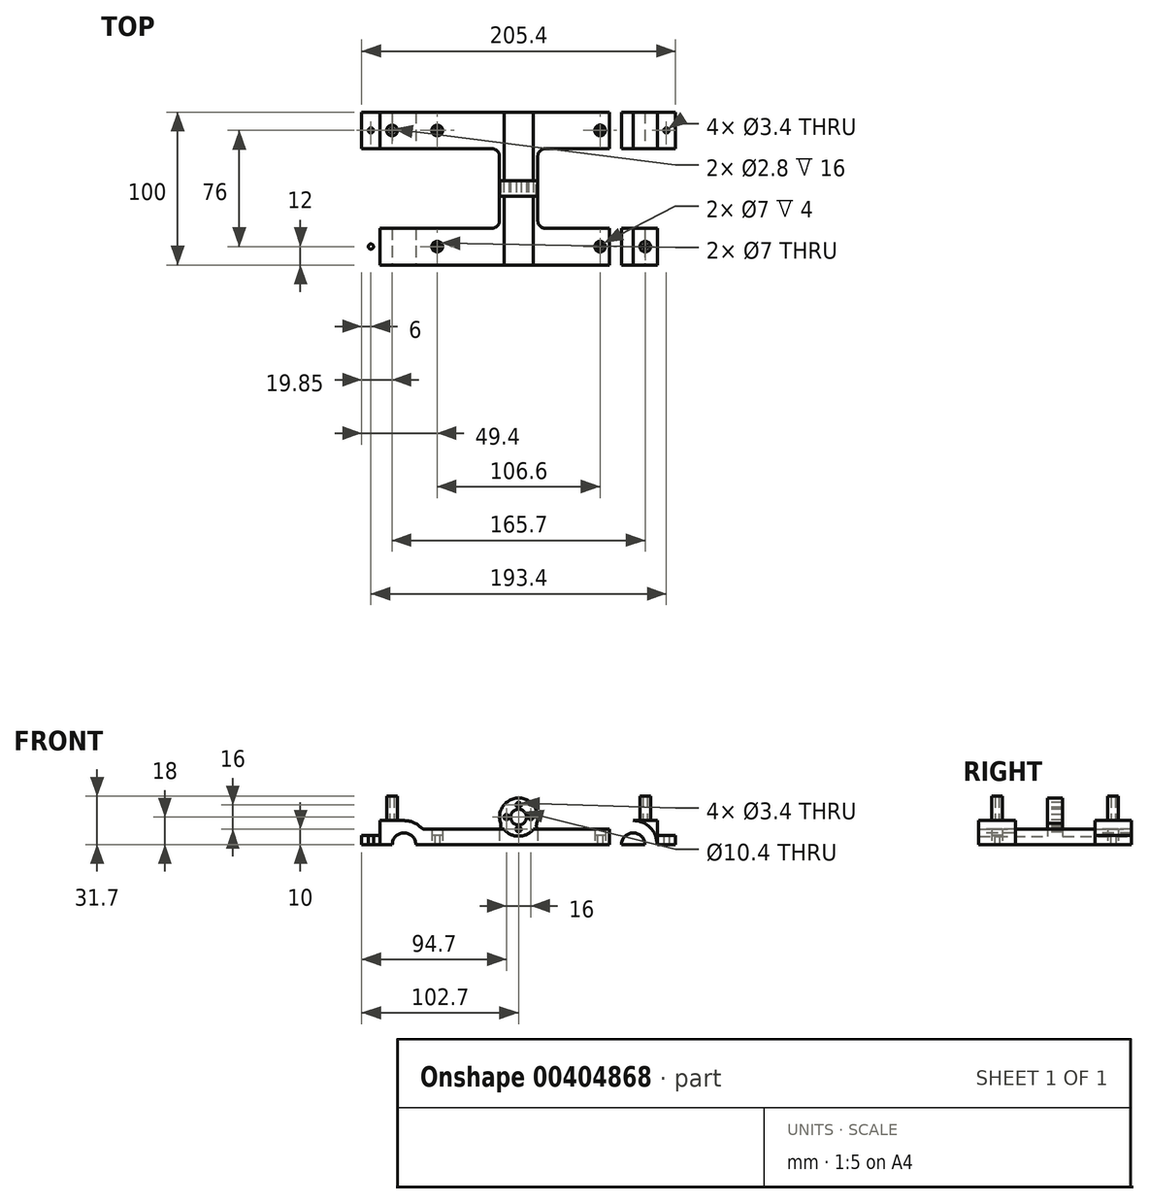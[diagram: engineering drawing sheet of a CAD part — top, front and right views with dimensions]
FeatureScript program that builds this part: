
annotation { "Feature Type Name" : "Feature", "Feature Type Description" : "" }
export const myFeature = defineFeature(function(context is Context, id is Id, definition is map)
    precondition{}
    {
        {
            var Q0;
            Q0=qCreatedBy(makeId("Top.planeOp"),FACE);
            var sketch = newSketch(context, id + "F0", { "sketchPlane" : qUnion([Q0])});
            skLineSegment(sketch, "E0", {"start": v(0, 0) * mm, "end": v(0, 50) * mm, "construction": true});
            skLineSegment(sketch, "E1", {"start": v(0, 0) * mm, "end": v(0, -50) * mm, "construction": true});
            skLineSegment(sketch, "E2", {"start": v(0, 50) * mm, "end": v(-59.3, 50) * mm});
            skLineSegment(sketch, "E3", {"start": v(-59.3, 50) * mm, "end": v(-59.3, 26) * mm});
            skLineSegment(sketch, "E4.bottom", {"start": v(-59.3, 26) * mm, "end": v(-90.7, 26) * mm});
            skLineSegment(sketch, "E4.top", {"start": v(-59.3, 50) * mm, "end": v(-90.7, 50) * mm});
            skLineSegment(sketch, "E4.left", {"start": v(-59.3, 26) * mm, "end": v(-59.3, 50) * mm});
            skLineSegment(sketch, "E4.right", {"start": v(-90.7, 26) * mm, "end": v(-90.7, 50) * mm});
            skLineSegment(sketch, "E5", {"start": v(-59.3, 26) * mm, "end": v(-12.5, 26) * mm});
            skLineSegment(sketch, "E6", {"start": v(0, 0) * mm, "end": v(-12.5, 0) * mm, "construction": true});
            skLineSegment(sketch, "E7", {"start": v(-12.5, 0) * mm, "end": v(-12.5, 26) * mm});
            skLineSegment(sketch, "E8.MirrorCS", {"start": v(59.3, 50) * mm, "end": v(90.7, 50) * mm});
            skLineSegment(sketch, "E9.MirrorCS", {"start": v(90.7, 26) * mm, "end": v(90.7, 50) * mm});
            skLineSegment(sketch, "E10.MirrorCS", {"start": v(59.3, 26) * mm, "end": v(90.7, 26) * mm});
            skLineSegment(sketch, "E11.MirrorCS", {"start": v(59.3, 26) * mm, "end": v(59.3, 50) * mm});
            skLineSegment(sketch, "E12.MirrorCS", {"start": v(59.3, 26) * mm, "end": v(12.5, 26) * mm});
            skLineSegment(sketch, "E13.MirrorCS", {"start": v(0, 50) * mm, "end": v(59.3, 50) * mm});
            skLineSegment(sketch, "E14.MirrorCS", {"start": v(12.5, 0) * mm, "end": v(12.5, 26) * mm});
            skLineSegment(sketch, "E15.MirrorCS", {"start": v(-12.5, 0) * mm, "end": v(-12.5, -26) * mm});
            skLineSegment(sketch, "E16.MirrorCS", {"start": v(-59.3, -26) * mm, "end": v(-12.5, -26) * mm});
            skLineSegment(sketch, "E17.MirrorCS", {"start": v(-59.3, -26) * mm, "end": v(-90.7, -26) * mm});
            skLineSegment(sketch, "E18.MirrorCS", {"start": v(-90.7, -26) * mm, "end": v(-90.7, -50) * mm});
            skLineSegment(sketch, "E19.MirrorCS", {"start": v(-59.3, -50) * mm, "end": v(-90.7, -50) * mm});
            skLineSegment(sketch, "E20.MirrorCS", {"start": v(-59.3, -26) * mm, "end": v(-59.3, -50) * mm});
            skLineSegment(sketch, "E21.MirrorCS", {"start": v(0, -50) * mm, "end": v(-59.3, -50) * mm});
            skLineSegment(sketch, "E22.MirrorCS", {"start": v(0, -50) * mm, "end": v(59.3, -50) * mm});
            skLineSegment(sketch, "E23.MirrorCS", {"start": v(59.3, -26) * mm, "end": v(12.5, -26) * mm});
            skLineSegment(sketch, "E24.MirrorCS", {"start": v(12.5, 0) * mm, "end": v(12.5, -26) * mm});
            skLineSegment(sketch, "E25.MirrorCS", {"start": v(59.3, -26) * mm, "end": v(90.7, -26) * mm});
            skLineSegment(sketch, "E26.MirrorCS", {"start": v(59.3, -26) * mm, "end": v(59.3, -50) * mm});
            skLineSegment(sketch, "E27.MirrorCS", {"start": v(59.3, -50) * mm, "end": v(90.7, -50) * mm});
            skLineSegment(sketch, "E28.MirrorCS", {"start": v(90.7, -26) * mm, "end": v(90.7, -50) * mm});
            skLineSegment(sketch, "E29.bottom", {"start": v(-12.5, 5) * mm, "end": v(12.5, 5) * mm});
            skLineSegment(sketch, "E29.top", {"start": v(-12.5, -5) * mm, "end": v(12.5, -5) * mm});
            skLineSegment(sketch, "E29.left", {"start": v(-12.5, 5) * mm, "end": v(-12.5, -5) * mm});
            skLineSegment(sketch, "E29.right", {"start": v(12.5, 5) * mm, "end": v(12.5, -5) * mm});
            skPoint(sketch, "E29.middle", {"position": v(0, 0) * mm});
            skLineSegment(sketch, "E30.bottom", {"start": v(-90.7, 50) * mm, "end": v(-102.7, 50) * mm});
            skLineSegment(sketch, "E30.top", {"start": v(-90.7, 26) * mm, "end": v(-102.7, 26) * mm});
            skLineSegment(sketch, "E30.left", {"start": v(-90.7, 50) * mm, "end": v(-90.7, 26) * mm});
            skLineSegment(sketch, "E30.right", {"start": v(-102.7, 50) * mm, "end": v(-102.7, 26) * mm});
            skCircle(sketch, "E31", {"center": v(-96.7, 38) * mm, "radius": 1.7 * mm});
            skPoint(sketch, "E31.centerSnap0", {"position": v(-90.7, 38) * mm});
            skPoint(sketch, "E31.centerSnap1", {"position": v(-96.7, 50) * mm});
            skLineSegment(sketch, "E32.MirrorCS", {"start": v(90.7, 50) * mm, "end": v(102.7, 50) * mm});
            skLineSegment(sketch, "E33.MirrorCS", {"start": v(102.7, 50) * mm, "end": v(102.7, 26) * mm});
            skLineSegment(sketch, "E34.MirrorCS", {"start": v(90.7, 26) * mm, "end": v(102.7, 26) * mm});
            skLineSegment(sketch, "E35.MirrorCS", {"start": v(90.7, 50) * mm, "end": v(90.7, 26) * mm});
            skCircle(sketch, "E36.MirrorC", {"center": v(96.7, 38) * mm, "radius": 1.7 * mm});
            skCircle(sketch, "E37.MirrorC", {"center": v(-96.7, -38) * mm, "radius": 1.7 * mm});
            skLineSegment(sketch, "E38.MirrorCS", {"start": v(-90.7, -50) * mm, "end": v(-90.7, -26) * mm});
            skLineSegment(sketch, "E39.MirrorCS", {"start": v(-90.7, -50) * mm, "end": v(-102.7, -50) * mm});
            skLineSegment(sketch, "E40.MirrorCS", {"start": v(-102.7, -50) * mm, "end": v(-102.7, -26) * mm});
            skLineSegment(sketch, "E41.MirrorCS", {"start": v(-90.7, -26) * mm, "end": v(-102.7, -26) * mm});
            skLineSegment(sketch, "E42.MirrorCS", {"start": v(90.7, -50) * mm, "end": v(90.7, -26) * mm});
            skLineSegment(sketch, "E43.MirrorCS", {"start": v(90.7, -50) * mm, "end": v(102.7, -50) * mm});
            skLineSegment(sketch, "E44.MirrorCS", {"start": v(102.7, -50) * mm, "end": v(102.7, -26) * mm});
            skLineSegment(sketch, "E45.MirrorCS", {"start": v(90.7, -26) * mm, "end": v(102.7, -26) * mm});
            skCircle(sketch, "E46.MirrorC", {"center": v(96.7, -38) * mm, "radius": 1.7 * mm});
            skLineSegment(sketch, "E47", {"start": v(-59.3, 38) * mm, "end": v(-53.3, 38) * mm, "construction": true});
            skCircle(sketch, "E48", {"center": v(-53.3, 38) * mm, "radius": 1.7 * mm});
            skCircle(sketch, "E49.MirrorC", {"center": v(53.3, 38) * mm, "radius": 1.7 * mm});
            skCircle(sketch, "E50.MirrorC", {"center": v(-53.3, -38) * mm, "radius": 1.7 * mm});
            skCircle(sketch, "E51.MirrorC", {"center": v(53.3, -38) * mm, "radius": 1.7 * mm});
            skCircle(sketch, "E52", {"center": v(-53.3, 38) * mm, "radius": 3.5 * mm});
            skCircle(sketch, "E53.MirrorC", {"center": v(53.3, 38) * mm, "radius": 3.5 * mm});
            skCircle(sketch, "E54.MirrorC", {"center": v(-53.3, -38) * mm, "radius": 3.5 * mm});
            skCircle(sketch, "E55.MirrorC", {"center": v(53.3, -38) * mm, "radius": 3.5 * mm});
            skSolve(sketch);
        }
        {
            var Q0;
            Q0=makeQuery(id+"F0.imprint","IMPRINT",FACE,{"disambiguationData":[TD([[makeQuery(id+"F0.imprint","IMPRINT",EDGE,{"derivedFrom":sQuery(id+"F0.wireOp",EDGE,"E2")}),1.0]])]});
            var Q1;
            Q1=makeQuery(id+"F0.imprint","IMPRINT",FACE,{"disambiguationData":[TD([[makeQuery(id+"F0.imprint","IMPRINT",EDGE,{"derivedFrom":sQuery(id+"F0.wireOp",EDGE,"E15.MirrorCS")}),1.0]])]});
            extrude(context, id + "F1", {"entities" : qUnion([Q0, Q1]), "depth" : 10 * mm});
        }
        {
            var Q0;
            Q0=makeQuery(id+"F0.imprint","IMPRINT",FACE,{"disambiguationData":[TD([[makeQuery(id+"F0.imprint","IMPRINT",EDGE,{"derivedFrom":sQuery(id+"F0.wireOp",EDGE,"E17.MirrorCS")}),1.0]])]});
            var Q1;
            Q1=makeQuery(id+"F0.imprint","IMPRINT",FACE,{"disambiguationData":[TD([[makeQuery(id+"F0.imprint","IMPRINT",EDGE,{"derivedFrom":sQuery(id+"F0.wireOp",EDGE,"E4.bottom")}),-1.0]])]});
            var Q2;
            Q2=makeQuery(id+"F0.imprint","IMPRINT",FACE,{"disambiguationData":[TD([[makeQuery(id+"F0.imprint","IMPRINT",EDGE,{"derivedFrom":sQuery(id+"F0.wireOp",EDGE,"E8.MirrorCS")}),-1.0]])]});
            var Q3;
            Q3=makeQuery(id+"F0.imprint","IMPRINT",FACE,{"disambiguationData":[TD([[makeQuery(id+"F0.imprint","IMPRINT",EDGE,{"derivedFrom":sQuery(id+"F0.wireOp",EDGE,"E25.MirrorCS")}),-1.0]])]});
            extrude(context, id + "F2", {"entities" : qUnion([Q0, Q1, Q2, Q3]), "depth" : 15.7 * mm});
        }
        {
            var Q0;
            Q0=makeQuery(id+"F0.imprint","IMPRINT",FACE,{"disambiguationData":[TD([[makeQuery(id+"F0.imprint","IMPRINT",EDGE,{"derivedFrom":sQuery(id+"F0.wireOp",EDGE,"E29.bottom")}),-1.0]])]});
            extrude(context, id + "F3", {"entities" : qUnion([Q0]), "depth" : 30.5 * mm});
        }
        {
            var Q0;
            Q0=makeQuery(id+"F2.opExtrude","SWEPT_BODY",BODY,{"disambiguationData":[OSD([sQuery(id+"F0.wireOp",EDGE,"E25.MirrorCS"),sQuery(id+"F0.wireOp",EDGE,"E26.MirrorCS"),sQuery(id+"F0.wireOp",EDGE,"E27.MirrorCS"),sQuery(id+"F0.wireOp",EDGE,"E28.MirrorCS")])]});
            var Q1;
            Q1=makeQuery(id+"F2.opExtrude","SWEPT_BODY",BODY,{"disambiguationData":[OSD([sQuery(id+"F0.wireOp",EDGE,"E4.bottom"),sQuery(id+"F0.wireOp",EDGE,"E4.top"),sQuery(id+"F0.wireOp",EDGE,"E4.left"),sQuery(id+"F0.wireOp",EDGE,"E4.right")])]});
            var Q2;
            Q2=makeQuery(id+"F2.opExtrude","SWEPT_BODY",BODY,{"disambiguationData":[OSD([sQuery(id+"F0.wireOp",EDGE,"E17.MirrorCS"),sQuery(id+"F0.wireOp",EDGE,"E18.MirrorCS"),sQuery(id+"F0.wireOp",EDGE,"E19.MirrorCS"),sQuery(id+"F0.wireOp",EDGE,"E20.MirrorCS")])]});
            var Q3;
            Q3=makeQuery(id+"F1.opExtrude","SWEPT_BODY",BODY,{"disambiguationData":[OSD([sQuery(id+"F0.wireOp",EDGE,"E2"),sQuery(id+"F0.wireOp",EDGE,"E4.left"),sQuery(id+"F0.wireOp",EDGE,"E5"),sQuery(id+"F0.wireOp",EDGE,"E7"),sQuery(id+"F0.wireOp",EDGE,"E11.MirrorCS"),sQuery(id+"F0.wireOp",EDGE,"E12.MirrorCS"),sQuery(id+"F0.wireOp",EDGE,"E13.MirrorCS"),sQuery(id+"F0.wireOp",EDGE,"E14.MirrorCS"),sQuery(id+"F0.wireOp",EDGE,"E29.bottom")])]});
            var Q4;
            Q4=makeQuery(id+"F1.opExtrude","SWEPT_BODY",BODY,{"disambiguationData":[OSD([sQuery(id+"F0.wireOp",EDGE,"E15.MirrorCS"),sQuery(id+"F0.wireOp",EDGE,"E16.MirrorCS"),sQuery(id+"F0.wireOp",EDGE,"E20.MirrorCS"),sQuery(id+"F0.wireOp",EDGE,"E21.MirrorCS"),sQuery(id+"F0.wireOp",EDGE,"E22.MirrorCS"),sQuery(id+"F0.wireOp",EDGE,"E23.MirrorCS"),sQuery(id+"F0.wireOp",EDGE,"E24.MirrorCS"),sQuery(id+"F0.wireOp",EDGE,"E26.MirrorCS"),sQuery(id+"F0.wireOp",EDGE,"E29.top")])]});
            var Q5;
            Q5=makeQuery(id+"F3.opExtrude","SWEPT_BODY",BODY,{"disambiguationData":[OSD([sQuery(id+"F0.wireOp",EDGE,"E29.bottom"),sQuery(id+"F0.wireOp",EDGE,"E29.top"),sQuery(id+"F0.wireOp",EDGE,"E29.left"),sQuery(id+"F0.wireOp",EDGE,"E29.right")])]});
            var Q6;
            Q6=makeQuery(id+"F2.opExtrude","SWEPT_BODY",BODY,{"disambiguationData":[OSD([sQuery(id+"F0.wireOp",EDGE,"E8.MirrorCS"),sQuery(id+"F0.wireOp",EDGE,"E9.MirrorCS"),sQuery(id+"F0.wireOp",EDGE,"E10.MirrorCS"),sQuery(id+"F0.wireOp",EDGE,"E11.MirrorCS")])]});
            booleanBodies(context, id + "F4", {"operationType" : BooleanOperationType.UNION, "tools" : qUnion([Q0, Q1, Q2, Q3, Q4, Q5, Q6])});
        }
        {
            var Q0;
            Q0=makeQuery(id+"F4.opBoolean","MERGE",FACE,{"derivedFrom":[makeQuery(id+"F1.opExtrude","SWEPT_FACE",FACE,{"disambiguationData":[OSD([sQuery(id+"F0.wireOp",EDGE,"E21.MirrorCS"),sQuery(id+"F0.wireOp",EDGE,"E22.MirrorCS")])]}),makeQuery(id+"F2.opExtrude","SWEPT_FACE",FACE,{"disambiguationData":[OSD([sQuery(id+"F0.wireOp",EDGE,"E19.MirrorCS")])]}),makeQuery(id+"F2.opExtrude","SWEPT_FACE",FACE,{"disambiguationData":[OSD([sQuery(id+"F0.wireOp",EDGE,"E27.MirrorCS")])]})]});
            var sketch = newSketch(context, id + "F5", { "sketchPlane" : qUnion([Q0])});
            skLineSegment(sketch, "E56", {"start": v(-75, 15.7) * mm, "end": v(-75, 0) * mm, "construction": true});
            skArc(sketch, "E57", {"start": v(-64.07, 11.27) * mm, "mid": v(-81.12, 14.46) * mm, "end": v(-90.7, 0) * mm});
            skArc(sketch, "E58", {"start": v(-67.3, 0) * mm, "mid": v(-75, 7.7) * mm, "end": v(-82.7, 0) * mm});
            skLineSegment(sketch, "E59", {"start": v(-82.7, 0) * mm, "end": v(-90.7, 0) * mm});
            skLineSegment(sketch, "E60", {"start": v(-67.3, 0) * mm, "end": v(-59.3, 0) * mm});
            skLineSegment(sketch, "E61", {"start": v(0, 0) * mm, "end": v(0, 35.4) * mm, "construction": true});
            skPoint(sketch, "E61.endSnap0", {"position": v(0, 0) * mm});
            skArc(sketch, "E62.MirrorCS", {"start": v(67.3, 0) * mm, "mid": v(75, 7.7) * mm, "end": v(82.7, 0) * mm});
            skLineSegment(sketch, "E63.MirrorCS", {"start": v(82.7, 0) * mm, "end": v(90.7, 0) * mm});
            skArc(sketch, "E64.MirrorCS", {"start": v(64.07, 11.27) * mm, "mid": v(81.12, 14.46) * mm, "end": v(90.7, 0) * mm});
            skLineSegment(sketch, "E65.MirrorCS", {"start": v(67.3, 0) * mm, "end": v(59.3, 0) * mm});
            skLineSegment(sketch, "E66", {"start": v(-59.3, 0) * mm, "end": v(-59.3, 15.7) * mm});
            skLineSegment(sketch, "E67", {"start": v(-59.3, 15.7) * mm, "end": v(-75, 15.7) * mm});
            skLineSegment(sketch, "E68.MirrorCS", {"start": v(59.3, 15.7) * mm, "end": v(75, 15.7) * mm});
            skLineSegment(sketch, "E69.MirrorCS", {"start": v(59.3, 0) * mm, "end": v(59.3, 15.7) * mm});
            skLineSegment(sketch, "E70", {"start": v(-59.3, 10) * mm, "end": v(-60.94, 10) * mm});
            skPoint(sketch, "E71.newPointA", {"position": v(-59.3, 0) * mm});
            skArc(sketch, "E71.filletArc", {"start": v(-64.07, 11.27) * mm, "mid": v(-62.63, 10.33) * mm, "end": v(-60.94, 10) * mm});
            skLineSegment(sketch, "E72", {"start": v(59.3, 10) * mm, "end": v(60.94, 10) * mm});
            skPoint(sketch, "E73.newPointB", {"position": v(59.3, 0) * mm});
            skArc(sketch, "E73.filletArc", {"start": v(60.94, 10) * mm, "mid": v(62.63, 10.33) * mm, "end": v(64.07, 11.27) * mm});
            skSolve(sketch);
        }
        {
            var Q0;
            {var subQ6=sQuery(id+"F5.wireOp",EDGE,"E68.MirrorCS");Q0=makeQuery(id+"F5.imprint","IMPRINT",FACE,{"disambiguationData":[TD([[makeQuery(id+"F5.imprint","IMPRINT",EDGE,{"derivedFrom":subQ6}),-1.0]])]});}
            var Q1;
            {var subQ0=sQuery(id+"F5.wireOp",EDGE,"8ee72258-81a3-4149-ab89-0d706ac254500.MirrorCS");Q1=makeQuery(id+"F5.imprint","IMPRINT",FACE,{"disambiguationData":[TD([[makeQuery(id+"F5.imprint","IMPRINT",EDGE,{"derivedFrom":subQ0}),-1.0]])]});}
            var Q2;
            {var subQ0=sQuery(id+"F5.wireOp",EDGE,"E62.MirrorCS");Q2=makeQuery(id+"F5.imprint","IMPRINT",FACE,{"disambiguationData":[TD([[makeQuery(id+"F5.imprint","IMPRINT",EDGE,{"derivedFrom":subQ0}),-1.0]])]});}
            var Q3;
            {var subQ0=sQuery(id+"F5.wireOp",EDGE,"2AFTPnqg-4Tv1-YmLw-YE9B-kkPoXeHdkq1D");Q3=makeQuery(id+"F5.imprint","IMPRINT",FACE,{"disambiguationData":[TD([[makeQuery(id+"F5.imprint","IMPRINT",EDGE,{"derivedFrom":subQ0}),1.0]])]});}
            var Q4;
            {var subQ6=sQuery(id+"F5.wireOp",EDGE,"E67");Q4=makeQuery(id+"F5.imprint","IMPRINT",FACE,{"disambiguationData":[TD([[makeQuery(id+"F5.imprint","IMPRINT",EDGE,{"derivedFrom":subQ6}),1.0]])]});}
            var Q5;
            {var subQ0=sQuery(id+"F5.wireOp",EDGE,"E58");Q5=makeQuery(id+"F5.imprint","IMPRINT",FACE,{"disambiguationData":[TD([[makeQuery(id+"F5.imprint","IMPRINT",EDGE,{"derivedFrom":subQ0}),1.0]])]});}
            extrude(context, id + "F6", {"entities" : qUnion([Q0, Q1, Q2, Q3, Q4, Q5]), "operationType" : NewBodyOperationType.REMOVE, "oppositeDirection" : true, "depth" : 100 * mm});
        }
        {
            var Q0;
            Q0=makeQuery(id+"F3.opExtrude","SWEPT_FACE",FACE,{"disambiguationData":[OSD([sQuery(id+"F0.wireOp",EDGE,"E29.top")])]});
            var sketch = newSketch(context, id + "F7", { "sketchPlane" : qUnion([Q0])});
            skLineSegment(sketch, "E74", {"start": v(0, 0) * mm, "end": v(0, 18) * mm, "construction": true});
            skFitSpline(sketch, "E75", {"points": [v(-11.82, 13.93) * mm, v(-11.66, 11.67) * mm, v(-12.5, 10) * mm], "startDerivative": vector(0.82, -4.52) * mm, "endDerivative": vector(-2.25, -3.32) * mm});
            skFitSpline(sketch, "E76.MirrorCS", {"points": [v(11.82, 13.93) * mm, v(11.66, 11.67) * mm, v(12.5, 10) * mm], "startDerivative": vector(-0.82, -4.52) * mm, "endDerivative": vector(2.25, -3.32) * mm});
            skCircle(sketch, "E77", {"center": v(0, 18) * mm, "radius": 5.2 * mm});
            skCircle(sketch, "E78", {"center": v(0, 18) * mm, "radius": 8 * mm, "construction": true});
            skArc(sketch, "E79", {"start": v(11.82, 13.93) * mm, "mid": v(0, 30.5) * mm, "end": v(-11.82, 13.93) * mm});
            skCircle(sketch, "E80", {"center": v(0, 26) * mm, "radius": 1.7 * mm});
            skCircle(sketch, "E81", {"center": v(8, 18) * mm, "radius": 1.7 * mm});
            skCircle(sketch, "E82", {"center": v(0, 10) * mm, "radius": 1.7 * mm});
            skCircle(sketch, "E83", {"center": v(-8, 18) * mm, "radius": 1.7 * mm});
            skLineSegment(sketch, "E84", {"start": v(-12.5, 10) * mm, "end": v(-9.6, 10) * mm});
            skLineSegment(sketch, "E85", {"start": v(12.5, 10) * mm, "end": v(9.6, 10) * mm});
            skArc(sketch, "E86.trimOffspring", {"start": v(-9.6, 10) * mm, "mid": v(0, 5.5) * mm, "end": v(9.6, 10) * mm});
            skSolve(sketch);
        }
        {
            var Q0;
            {var subQ0=sQuery(id+"F7.wireOp",EDGE,"E79");var subQ1=sQuery(id+"F0.wireOp",EDGE,"E29.top");var subQ2=makeQuery(id+"F3.opExtrude","CAP_EDGE",EDGE,{"disambiguationData":[OSD([subQ1])],"isStart":false});var subQ3=makeQuery(id+"F7.imprint","INTERSECT",VERTEX,{"derivedFrom":[subQ2,subQ0]});Q0=makeQuery(id+"F7.imprint","IMPRINT",FACE,{"disambiguationData":[TD([[makeQuery(id+"F7.imprint","IMPRINT",EDGE,{"disambiguationData":[TD([[subQ3,-1.0]])],"derivedFrom":subQ0}),-1.0]])]});}
            var Q1;
            {var subQ0=sQuery(id+"F7.wireOp",EDGE,"E79");var subQ1=sQuery(id+"F0.wireOp",EDGE,"E29.top");var subQ4=makeQuery(id+"F3.opExtrude","CAP_EDGE",EDGE,{"disambiguationData":[OSD([subQ1])],"isStart":false});var subQ5=makeQuery(id+"F7.imprint","INTERSECT",VERTEX,{"derivedFrom":[subQ4,subQ0]});Q1=makeQuery(id+"F7.imprint","IMPRINT",FACE,{"disambiguationData":[TD([[makeQuery(id+"F7.imprint","IMPRINT",EDGE,{"disambiguationData":[TD([[subQ5,1.0]])],"derivedFrom":subQ0}),-1.0]])]});}
            var Q2;
            {var subQ0=sQuery(id+"F7.wireOp",EDGE,"E75");Q2=makeQuery(id+"F7.imprint","IMPRINT",FACE,{"disambiguationData":[TD([[makeQuery(id+"F7.imprint","IMPRINT",EDGE,{"derivedFrom":subQ0}),-1.0]])]});}
            var Q3;
            {var subQ0=sQuery(id+"F7.wireOp",EDGE,"E76.MirrorCS");Q3=makeQuery(id+"F7.imprint","IMPRINT",FACE,{"disambiguationData":[TD([[makeQuery(id+"F7.imprint","IMPRINT",EDGE,{"derivedFrom":subQ0}),1.0]])]});}
            var Q4;
            Q4=makeQuery(id+"F7.imprint","IMPRINT",FACE,{"disambiguationData":[TD([[makeQuery(id+"F7.imprint","IMPRINT",EDGE,{"derivedFrom":sQuery(id+"F7.wireOp",EDGE,"E83")}),1.0]])]});
            var Q5;
            Q5=makeQuery(id+"F7.imprint","IMPRINT",FACE,{"disambiguationData":[TD([[makeQuery(id+"F7.imprint","IMPRINT",EDGE,{"derivedFrom":sQuery(id+"F7.wireOp",EDGE,"E80")}),1.0]])]});
            var Q6;
            Q6=makeQuery(id+"F7.imprint","IMPRINT",FACE,{"disambiguationData":[TD([[makeQuery(id+"F7.imprint","IMPRINT",EDGE,{"derivedFrom":sQuery(id+"F7.wireOp",EDGE,"E81")}),1.0]])]});
            var Q7;
            {var subQ0=sQuery(id+"F7.wireOp",EDGE,"E82");var subQ1=makeQuery(id+"F1.opExtrude","CAP_EDGE",EDGE,{"disambiguationData":[OSD([sQuery(id+"F0.wireOp",EDGE,"E29.top")])],"isStart":false});var subQ2=makeQuery(id+"F7.imprint","INTERSECT",VERTEX,{"disambiguationData":[OD(0.0)],"derivedFrom":[subQ1,subQ0]});Q7=makeQuery(id+"F7.imprint","IMPRINT",FACE,{"disambiguationData":[TD([[makeQuery(id+"F7.imprint","IMPRINT",EDGE,{"disambiguationData":[TD([[subQ2,1.0]])],"derivedFrom":subQ0}),1.0]])]});}
            var Q8;
            {var subQ0=sQuery(id+"F7.wireOp",EDGE,"E82");var subQ1=makeQuery(id+"F1.opExtrude","CAP_EDGE",EDGE,{"disambiguationData":[OSD([sQuery(id+"F0.wireOp",EDGE,"E29.top")])],"isStart":false});var subQ2=makeQuery(id+"F7.imprint","INTERSECT",VERTEX,{"disambiguationData":[OD(0.0)],"derivedFrom":[subQ1,subQ0]});Q8=makeQuery(id+"F7.imprint","IMPRINT",FACE,{"disambiguationData":[TD([[makeQuery(id+"F7.imprint","IMPRINT",EDGE,{"disambiguationData":[TD([[subQ2,-1.0]])],"derivedFrom":subQ0}),1.0]])]});}
            var Q9;
            Q9=makeQuery(id+"F7.imprint","IMPRINT",FACE,{"disambiguationData":[TD([[makeQuery(id+"F7.imprint","IMPRINT",EDGE,{"derivedFrom":sQuery(id+"F7.wireOp",EDGE,"E77")}),1.0]])]});
            extrude(context, id + "F8", {"entities" : qUnion([Q0, Q1, Q2, Q3, Q4, Q5, Q6, Q7, Q8, Q9]), "operationType" : NewBodyOperationType.REMOVE, "endBound" : BoundingType.SYMMETRIC, "oppositeDirection" : true, "depth" : 120 * mm});
        }
        {
            var Q0;
            {var subQ4=sQuery(id+"F7.wireOp",EDGE,"E86.trimOffspring");Q0=makeQuery(id+"F7.imprint","IMPRINT",FACE,{"disambiguationData":[TD([[makeQuery(id+"F7.imprint","IMPRINT",EDGE,{"derivedFrom":subQ4}),1.0]])]});}
            extrude(context, id + "F9", {"entities" : qUnion([Q0]), "operationType" : NewBodyOperationType.REMOVE, "depth" : 100 * mm});
        }
        {
            var Q0;
            {var subQ4=sQuery(id+"F7.wireOp",EDGE,"E86.trimOffspring");Q0=makeQuery(id+"F7.imprint","IMPRINT",FACE,{"disambiguationData":[TD([[makeQuery(id+"F7.imprint","IMPRINT",EDGE,{"derivedFrom":subQ4}),1.0]])]});}
            extrude(context, id + "F10", {"entities" : qUnion([Q0]), "operationType" : NewBodyOperationType.REMOVE, "oppositeDirection" : true, "depth" : 100 * mm});
        }
        {
            var Q0;
            {var subQ4=sQuery(id+"F7.wireOp",EDGE,"E86.trimOffspring");Q0=makeQuery(id+"F7.imprint","IMPRINT",FACE,{"disambiguationData":[TD([[makeQuery(id+"F7.imprint","IMPRINT",EDGE,{"derivedFrom":subQ4}),1.0]])]});}
            extrude(context, id + "F11", {"entities" : qUnion([Q0]), "operationType" : NewBodyOperationType.ADD, "oppositeDirection" : true, "depth" : 10 * mm});
        }
        {
            var Q0;
            Q0=makeQuery(id+"F1.opExtrude","SWEPT_EDGE",EDGE,{"disambiguationData":[OSD([sQuery(id+"F0.wireOp",EDGE,"E5"),sQuery(id+"F0.wireOp",EDGE,"E7")])]});
            var Q1;
            Q1=makeQuery(id+"F1.opExtrude","SWEPT_EDGE",EDGE,{"disambiguationData":[OSD([sQuery(id+"F0.wireOp",EDGE,"E12.MirrorCS"),sQuery(id+"F0.wireOp",EDGE,"E14.MirrorCS")])]});
            var Q2;
            Q2=makeQuery(id+"F1.opExtrude","SWEPT_EDGE",EDGE,{"disambiguationData":[OSD([sQuery(id+"F0.wireOp",EDGE,"E15.MirrorCS"),sQuery(id+"F0.wireOp",EDGE,"E16.MirrorCS")])]});
            var Q3;
            Q3=makeQuery(id+"F1.opExtrude","SWEPT_EDGE",EDGE,{"disambiguationData":[OSD([sQuery(id+"F0.wireOp",EDGE,"E23.MirrorCS"),sQuery(id+"F0.wireOp",EDGE,"E24.MirrorCS")])]});
            fillet(context, id + "F12", {"entities" : qUnion([Q0, Q1, Q2, Q3]), "radius" : 5 * mm, "tangentPropagation" : true, "allowEdgeOverflow" : false});
        }
        {
            var Q0;
            Q0=makeQuery(id+"F0.imprint","IMPRINT",FACE,{"disambiguationData":[TD([[makeQuery(id+"F0.imprint","IMPRINT",EDGE,{"derivedFrom":sQuery(id+"F0.wireOp",EDGE,"E30.bottom")}),1.0]])]});
            var Q1;
            Q1=makeQuery(id+"F0.imprint","IMPRINT",FACE,{"disambiguationData":[TD([[makeQuery(id+"F0.imprint","IMPRINT",EDGE,{"derivedFrom":sQuery(id+"F0.wireOp",EDGE,"E37.MirrorC")}),1.0]])]});
            var Q2;
            Q2=makeQuery(id+"F0.imprint","IMPRINT",FACE,{"disambiguationData":[TD([[makeQuery(id+"F0.imprint","IMPRINT",EDGE,{"derivedFrom":sQuery(id+"F0.wireOp",EDGE,"E42.MirrorCS")}),-1.0]])]});
            var Q3;
            Q3=makeQuery(id+"F0.imprint","IMPRINT",FACE,{"disambiguationData":[TD([[makeQuery(id+"F0.imprint","IMPRINT",EDGE,{"derivedFrom":sQuery(id+"F0.wireOp",EDGE,"E32.MirrorCS")}),-1.0]])]});
            extrude(context, id + "F13", {"entities" : qUnion([Q0, Q1, Q2, Q3]), "depth" : 6 * mm});
        }
        {
            var Q0;
            Q0=makeQuery(id+"F0.imprint","IMPRINT",FACE,{"disambiguationData":[TD([[makeQuery(id+"F0.imprint","IMPRINT",EDGE,{"derivedFrom":sQuery(id+"F0.wireOp",EDGE,"E48")}),-1.0]])]});
            var Q1;
            Q1=makeQuery(id+"F0.imprint","IMPRINT",FACE,{"disambiguationData":[TD([[makeQuery(id+"F0.imprint","IMPRINT",EDGE,{"derivedFrom":sQuery(id+"F0.wireOp",EDGE,"E49.MirrorC")}),1.0]])]});
            var Q2;
            Q2=makeQuery(id+"F0.imprint","IMPRINT",FACE,{"disambiguationData":[TD([[makeQuery(id+"F0.imprint","IMPRINT",EDGE,{"derivedFrom":sQuery(id+"F0.wireOp",EDGE,"E50.MirrorC")}),1.0]])]});
            var Q3;
            Q3=makeQuery(id+"F0.imprint","IMPRINT",FACE,{"disambiguationData":[TD([[makeQuery(id+"F0.imprint","IMPRINT",EDGE,{"derivedFrom":sQuery(id+"F0.wireOp",EDGE,"E51.MirrorC")}),-1.0]])]});
            extrude(context, id + "F14", {"entities" : qUnion([Q0, Q1, Q2, Q3]), "operationType" : NewBodyOperationType.ADD, "depth" : 6 * mm});
        }
        {
            var Q0;
            Q0=makeQuery(id+"F2.opExtrude","CAP_FACE",FACE,{"disambiguationData":[OSD([sQuery(id+"F0.wireOp",EDGE,"E4.bottom"),sQuery(id+"F0.wireOp",EDGE,"E4.top"),sQuery(id+"F0.wireOp",EDGE,"E4.left"),sQuery(id+"F0.wireOp",EDGE,"E30.left")])],"isStart":false});
            var sketch = newSketch(context, id + "F15", { "sketchPlane" : qUnion([Q0])});
            skLineSegment(sketch, "E87", {"start": v(-90.7, 50) * mm, "end": v(-75, 26) * mm, "construction": true});
            skLineSegment(sketch, "E88", {"start": v(-75, 50) * mm, "end": v(-90.7, 26) * mm, "construction": true});
            skCircle(sketch, "E89", {"center": v(-82.85, 38) * mm, "radius": 3.5 * mm});
            skLineSegment(sketch, "E90", {"start": v(0, 0) * mm, "end": v(0, 47.66) * mm, "construction": true});
            skLineSegment(sketch, "E91", {"start": v(0, 0) * mm, "end": v(-18.82, 0) * mm, "construction": true});
            skCircle(sketch, "E92.MirrorC", {"center": v(82.85, 38) * mm, "radius": 3.5 * mm});
            skCircle(sketch, "E93.MirrorC", {"center": v(-82.85, -38) * mm, "radius": 3.5 * mm});
            skCircle(sketch, "E94.MirrorC", {"center": v(82.85, -38) * mm, "radius": 3.5 * mm});
            skCircle(sketch, "E95", {"center": v(-82.85, -38) * mm, "radius": 1.4 * mm});
            skCircle(sketch, "E96.MirrorC", {"center": v(82.85, -38) * mm, "radius": 1.4 * mm});
            skCircle(sketch, "E97.MirrorC", {"center": v(-82.85, 38) * mm, "radius": 1.4 * mm});
            skCircle(sketch, "E98.MirrorC", {"center": v(82.85, 38) * mm, "radius": 1.4 * mm});
            skSolve(sketch);
        }
        {
            var Q0;
            Q0=makeQuery(id+"F15.imprint","IMPRINT",FACE,{"disambiguationData":[TD([[makeQuery(id+"F15.imprint","IMPRINT",EDGE,{"derivedFrom":sQuery(id+"F15.wireOp",EDGE,"E89")}),1.0]])]});
            var Q1;
            Q1=makeQuery(id+"F15.imprint","IMPRINT",FACE,{"disambiguationData":[TD([[makeQuery(id+"F15.imprint","IMPRINT",EDGE,{"derivedFrom":sQuery(id+"F15.wireOp",EDGE,"E92.MirrorC")}),-1.0]])]});
            var Q2;
            Q2=makeQuery(id+"F15.imprint","IMPRINT",FACE,{"disambiguationData":[TD([[makeQuery(id+"F15.imprint","IMPRINT",EDGE,{"derivedFrom":sQuery(id+"F15.wireOp",EDGE,"E94.MirrorC")}),1.0]])]});
            var Q3;
            Q3=makeQuery(id+"F15.imprint","IMPRINT",FACE,{"disambiguationData":[TD([[makeQuery(id+"F15.imprint","IMPRINT",EDGE,{"derivedFrom":sQuery(id+"F15.wireOp",EDGE,"E93.MirrorC")}),-1.0]])]});
            extrude(context, id + "F16", {"entities" : qUnion([Q0, Q1, Q2, Q3]), "operationType" : NewBodyOperationType.ADD, "depth" : 16 * mm});
        }
    });
